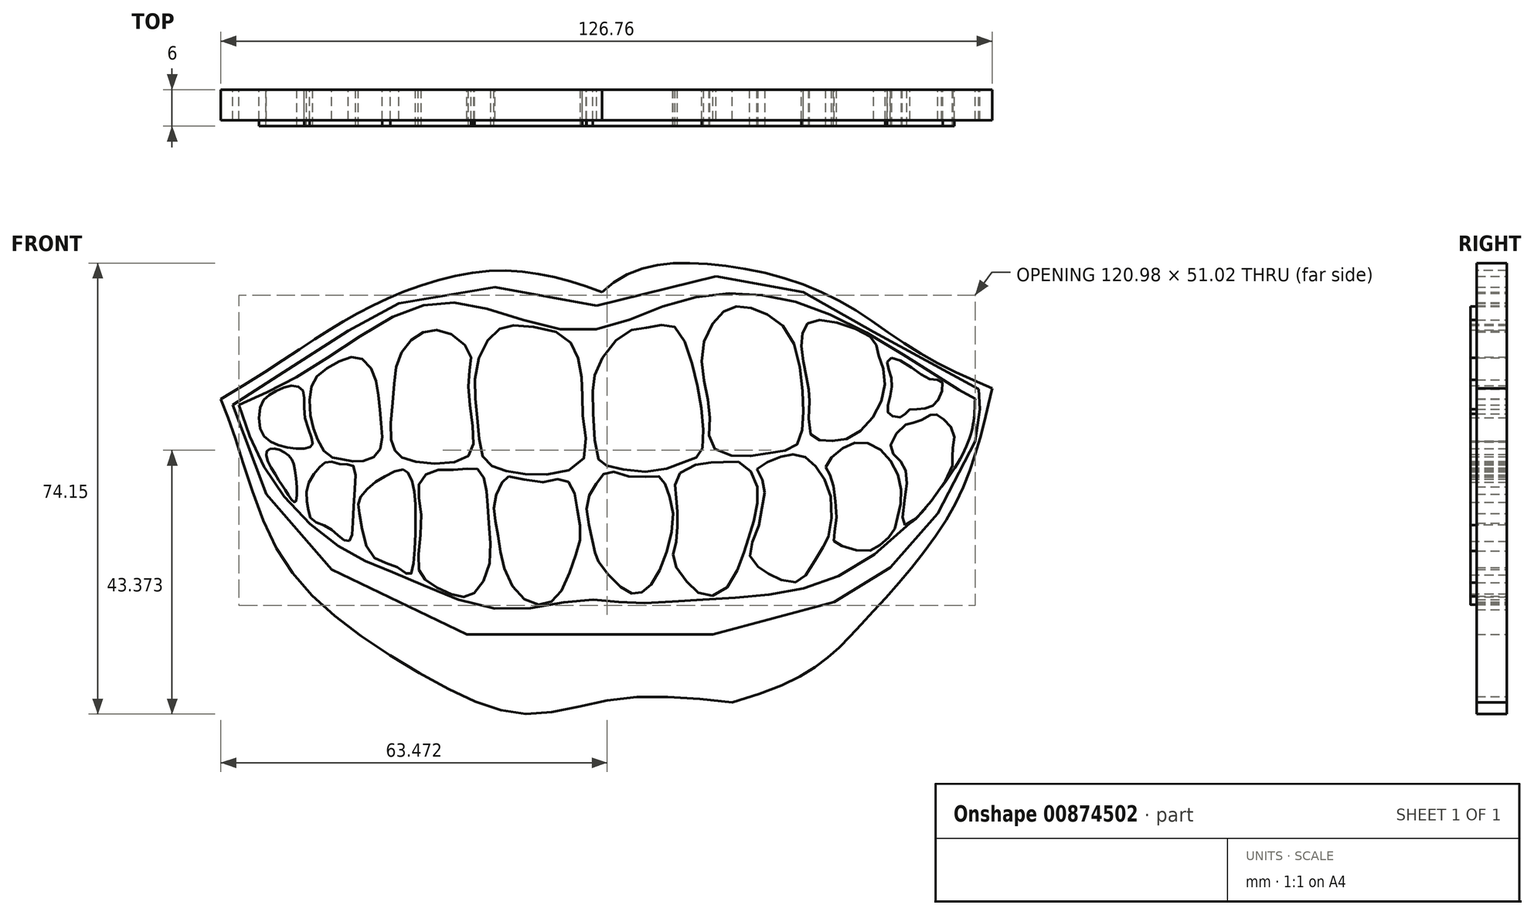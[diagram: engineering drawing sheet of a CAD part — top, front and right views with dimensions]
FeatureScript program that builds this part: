
annotation { "Feature Type Name" : "Feature", "Feature Type Description" : "" }
export const myFeature = defineFeature(function(context is Context, id is Id, definition is map)
    precondition{}
    {
        {
            var Q0;
            Q0=qCreatedBy(makeId("Front.planeOp"),FACE);
            var sketch = newSketch(context, id + "F0", { "sketchPlane" : qUnion([Q0])});
            skFitSpline(sketch, "E0", {"points": [v(0, 53.18) * mm, v(23.75, 67.94) * mm, v(44.07, 74.21) * mm, v(62.66, 70.72) * mm], "startDerivative": vector(93.7, 55.72) * mm, "endDerivative": vector(60.4, -23.03) * mm});
            skFitSpline(sketch, "E1", {"points": [v(126.76, 54.96) * mm, v(114.63, 60.86) * mm, v(103.77, 68.1) * mm, v(91.61, 73.34) * mm, v(78.85, 75.44) * mm, v(69.82, 74.76) * mm, v(62.66, 70.72) * mm], "startDerivative": vector(-69.64, 30.18) * mm, "endDerivative": vector(-38.87, -41.98) * mm});
            skFitSpline(sketch, "E2", {"points": [v(0, 53.18) * mm, v(2.98, 44.84) * mm, v(8.86, 29.1) * mm, v(20.03, 16.48) * mm, v(38.15, 5.15) * mm, v(51.1, 1.38) * mm, v(65.34, 3.9) * mm, v(84.07, 3.33) * mm], "startDerivative": vector(26.52, -69.74) * mm, "endDerivative": vector(123.22, -12.78) * mm});
            skFitSpline(sketch, "E3", {"points": [v(126.76, 54.96) * mm, v(120.46, 35.47) * mm, v(105, 15.84) * mm, v(84.07, 3.33) * mm], "startDerivative": vector(-14.9, -62.4) * mm, "endDerivative": vector(-111.82, -31.62) * mm});
            skFitSpline(sketch, "E4", {"points": [v(2.98, 52.18) * mm, v(14.75, 58.17) * mm, v(30, 67.51) * mm, v(42.1, 68.47) * mm, v(59.06, 64.37) * mm, v(73.77, 68.8) * mm, v(87.62, 70.4) * mm, v(102.75, 65.85) * mm, v(119.4, 55.87) * mm, v(123.96, 53.22) * mm], "startDerivative": vector(105.78, 47.4) * mm, "endDerivative": vector(55.85, -30.6) * mm});
            skFitSpline(sketch, "E5", {"points": [v(2.98, 52.18) * mm, v(8.53, 39.61) * mm, v(20.03, 28.54) * mm, v(30.2, 23.87) * mm, v(45.83, 18.63) * mm, v(59.41, 20.13) * mm, v(67.57, 19.64) * mm, v(77.35, 20.11) * mm, v(90.4, 21.05) * mm, v(106.3, 26.86) * mm, v(122.29, 44.84) * mm, v(123.96, 53.22) * mm], "startDerivative": vector(45.77, -138.86) * mm, "endDerivative": vector(2.36, 104.45) * mm});
            skSolve(sketch);
        }
        {
            var Q0;
            Q0=qSketchRegion(id+"F0",true);
            extrude(context, id + "F1", {"entities" : qUnion([Q0]), "depth" : 5 * mm, "offsetDistance" : 25 * mm});
        }
        {
            var Q0;
            Q0=qCreatedBy(makeId("Front.planeOp"),FACE);
            var sketch = newSketch(context, id + "F2", { "sketchPlane" : qUnion([Q0])});
            skFitSpline(sketch, "E6", {"points": [v(13.53, 54.53) * mm, v(13.72, 50.73) * mm, v(15.07, 46.21) * mm, v(14.78, 45.4) * mm, v(12.9, 45.02) * mm, v(9.13, 45.7) * mm, v(6.62, 47.84) * mm, v(6.75, 52.55) * mm, v(8.76, 54.31) * mm, v(11.77, 55.38) * mm, v(13.53, 54.53) * mm]});
            skFitSpline(sketch, "E7", {"points": [v(15.91, 46.46) * mm, v(17.67, 43.89) * mm, v(20.06, 43.26) * mm, v(22.32, 42.88) * mm, v(24.83, 43.48) * mm, v(26.34, 45.36) * mm, v(26.34, 49.16) * mm, v(25.91, 53.4) * mm, v(24.95, 57.73) * mm, v(22.6, 60.01) * mm, v(19.54, 59.41) * mm, v(16.05, 57.19) * mm, v(14.73, 54.54) * mm, v(14.85, 49.67) * mm, v(15.91, 46.46) * mm]});
            skFitSpline(sketch, "E8", {"points": [v(28.62, 44.69) * mm, v(29.89, 43.48) * mm, v(34.59, 42.6) * mm, v(40.26, 43.48) * mm, v(41.53, 46.18) * mm, v(40.86, 52.9) * mm, v(40.86, 57.98) * mm, v(40.94, 60.82) * mm, v(37.58, 63.95) * mm, v(34, 64.4) * mm, v(31, 62.61) * mm, v(28.91, 58.88) * mm, v(28.32, 53.8) * mm, v(27.87, 47.23) * mm, v(28.62, 44.69) * mm]});
            skFitSpline(sketch, "E9", {"points": [v(44.52, 42.15) * mm, v(48.03, 41.1) * mm, v(54.6, 40.88) * mm, v(59.68, 43.48) * mm, v(59.53, 50.07) * mm, v(59.38, 55.52) * mm, v(58.48, 60.67) * mm, v(55.8, 63.88) * mm, v(48.94, 65.26) * mm, v(45.8, 64.69) * mm, v(42.94, 61.26) * mm, v(41.71, 55.2) * mm, v(42.18, 49.9) * mm, v(42.88, 44.16) * mm, v(44.52, 42.15) * mm]});
            skFitSpline(sketch, "E10", {"points": [v(62.1, 43.24) * mm, v(63.7, 42.16) * mm, v(70.98, 41.29) * mm, v(76.92, 43.14) * mm, v(78.87, 44.25) * mm, v(79.15, 50) * mm, v(77.48, 58.9) * mm, v(74.32, 65.2) * mm, v(70.8, 65.02) * mm, v(66.53, 64.1) * mm, v(61.8, 58.16) * mm, v(61.16, 52.97) * mm, v(62.1, 43.24) * mm]});
            skFitSpline(sketch, "E11", {"points": [v(84.75, 68.4) * mm, v(81.88, 66.9) * mm, v(79.19, 61.72) * mm, v(79.56, 55.52) * mm, v(80.4, 49.9) * mm, v(80.67, 45.49) * mm, v(85.3, 43.73) * mm, v(90.69, 44.38) * mm, v(94.4, 45.4) * mm, v(95.6, 48.73) * mm, v(95.51, 55.52) * mm, v(93.28, 64.1) * mm, v(88.46, 67.65) * mm, v(84.75, 68.4) * mm]});
            skFitSpline(sketch, "E12", {"points": [v(96.73, 52.86) * mm, v(97, 47.25) * mm, v(99.29, 46.31) * mm, v(103.34, 46.8) * mm, v(107.76, 51.18) * mm, v(109.12, 56.92) * mm, v(107.97, 60.88) * mm, v(107.42, 62.7) * mm, v(102.85, 65.25) * mm, v(97.09, 66) * mm, v(95.6, 64.1) * mm, v(95.6, 60.25) * mm, v(96.52, 55.52) * mm, v(96.73, 52.86) * mm]});
            skFitSpline(sketch, "E13", {"points": [v(110.18, 59.97) * mm, v(114.14, 57.92) * mm, v(117.02, 56.33) * mm, v(118.46, 56.1) * mm, v(118.25, 53.68) * mm, v(116.74, 51.94) * mm, v(114.5, 51.53) * mm, v(112.9, 51.3) * mm, v(112, 50.26) * mm, v(110.2, 50.45) * mm, v(109.56, 51.32) * mm, v(110.06, 53.92) * mm, v(110.15, 56.8) * mm, v(109.52, 59.03) * mm, v(110.18, 59.97) * mm]});
            skFitSpline(sketch, "E14", {"points": [v(11.17, 43.89) * mm, v(12.2, 41.1) * mm, v(12.24, 36.22) * mm, v(11.06, 37.44) * mm, v(9.13, 40.43) * mm, v(7.44, 44.3) * mm, v(8.64, 45.02) * mm, v(11.17, 43.89) * mm]});
            skFitSpline(sketch, "E15", {"points": [v(21.14, 29.83) * mm, v(21.72, 34.48) * mm, v(21.79, 42.16) * mm, v(20.1, 42.4) * mm, v(17.67, 42.88) * mm, v(16.05, 41.78) * mm, v(14.24, 38.78) * mm, v(14.3, 35.25) * mm, v(15.07, 33.28) * mm, v(17.67, 32.08) * mm, v(19.72, 30.35) * mm, v(21.14, 29.83) * mm]});
            skFitSpline(sketch, "E16", {"points": [v(30.73, 41.1) * mm, v(31.74, 38.4) * mm, v(31.98, 33.3) * mm, v(31.73, 26.51) * mm, v(31, 24.29) * mm, v(28.91, 25.6) * mm, v(24.83, 27.42) * mm, v(22.77, 34.48) * mm, v(22.7, 36.6) * mm, v(24.54, 38.83) * mm, v(27.44, 40.73) * mm, v(29.89, 41.6) * mm, v(30.73, 41.1) * mm]});
            skFitSpline(sketch, "E17", {"points": [v(42.2, 41.68) * mm, v(43.53, 39.08) * mm, v(43.93, 34.2) * mm, v(44.07, 25.72) * mm, v(41.16, 20.94) * mm, v(38.36, 20.92) * mm, v(33.92, 23.23) * mm, v(32.45, 25.84) * mm, v(32.94, 33.79) * mm, v(32.49, 38.99) * mm, v(34.7, 41.3) * mm, v(39.33, 41.6) * mm, v(42.2, 41.68) * mm]});
            skFitSpline(sketch, "E18", {"points": [v(47.25, 40.47) * mm, v(52.4, 39.48) * mm, v(55.99, 40.03) * mm, v(57.7, 38.78) * mm, v(58.62, 34.68) * mm, v(59.1, 30.71) * mm, v(58.05, 26.74) * mm, v(55.52, 21) * mm, v(52.99, 19.42) * mm, v(49.52, 20.54) * mm, v(46.48, 25.63) * mm, v(45.68, 30.17) * mm, v(44.97, 33.94) * mm, v(45.02, 36.7) * mm, v(46.29, 39.65) * mm, v(47.25, 40.47) * mm]});
            skFitSpline(sketch, "E19", {"points": [v(62.1, 26.4) * mm, v(65.59, 22.35) * mm, v(68.22, 21.16) * mm, v(70.18, 22.1) * mm, v(72.87, 26.9) * mm, v(74.31, 34.2) * mm, v(73.13, 38.88) * mm, v(72.04, 40.46) * mm, v(67.8, 40.35) * mm, v(63.63, 41.25) * mm, v(62, 39.64) * mm, v(60.28, 36.67) * mm, v(60.56, 32.18) * mm, v(61.47, 28.08) * mm, v(62.1, 26.4) * mm]});
            skFitSpline(sketch, "E20", {"points": [v(75.5, 41.02) * mm, v(74.65, 38.62) * mm, v(74.97, 35.94) * mm, v(75.02, 32.76) * mm, v(74.73, 29.26) * mm, v(74.31, 26.9) * mm, v(76.28, 23.51) * mm, v(79.22, 20.96) * mm, v(82.79, 21.8) * mm, v(85.58, 26.9) * mm, v(86.81, 30.54) * mm, v(88.12, 35.59) * mm, v(87.94, 39.62) * mm, v(85.4, 42.75) * mm, v(82.06, 42.72) * mm, v(79.69, 42.72) * mm, v(75.5, 41.02) * mm]});
            skFitSpline(sketch, "E21", {"points": [v(88.12, 41.63) * mm, v(89.22, 39.45) * mm, v(89.15, 36.51) * mm, v(88.12, 31.49) * mm, v(86.94, 27.61) * mm, v(88.64, 25.34) * mm, v(90.8, 24.02) * mm, v(94.25, 23.02) * mm, v(96.37, 24.55) * mm, v(98.81, 28.54) * mm, v(99.9, 30.62) * mm, v(100.18, 37.32) * mm, v(98.19, 41.57) * mm, v(95.75, 43.77) * mm, v(93.22, 44.03) * mm, v(90.69, 43.13) * mm, v(88.12, 41.63) * mm]});
            skFitSpline(sketch, "E22", {"points": [v(99.44, 41.98) * mm, v(101.2, 44.38) * mm, v(104.48, 46.05) * mm, v(107.95, 45.2) * mm, v(110.88, 41.6) * mm, v(111.85, 37.32) * mm, v(111.18, 33.59) * mm, v(110.42, 31.17) * mm, v(108.52, 29.32) * mm, v(106.28, 28.2) * mm, v(102.13, 29.03) * mm, v(100.73, 29.97) * mm, v(101.09, 32.23) * mm, v(100.9, 37.32) * mm, v(100.18, 40.58) * mm, v(99.44, 41.98) * mm]});
            skFitSpline(sketch, "E23", {"points": [v(112.46, 32.44) * mm, v(120.07, 41.6) * mm, v(120.21, 44.38) * mm, v(120.43, 47.74) * mm, v(118.2, 50.28) * mm, v(117.02, 50.71) * mm, v(114.5, 49.43) * mm, v(112.66, 49) * mm, v(110.06, 45.2) * mm, v(111.85, 42.83) * mm, v(112.64, 38.24) * mm, v(112.46, 32.44) * mm]});
            skSolve(sketch);
        }
        {
            var Q0;
            Q0=qSketchRegion(id+"F2",true);
            extrude(context, id + "F3", {"entities" : qUnion([Q0]), "operationType" : NewBodyOperationType.ADD, "depth" : 6 * mm, "offsetDistance" : 25 * mm});
        }
        {
            var Q0;
            Q0=makeQuery(id+"F3.boolean.opBoolean","MERGE",FACE,{"derivedFrom":[makeQuery(id+"F1.opExtrude","CAP_FACE",FACE,{"disambiguationData":[OSD([sQuery(id+"F0.wireOp",EDGE,"E0"),sQuery(id+"F0.wireOp",EDGE,"E1"),sQuery(id+"F0.wireOp",EDGE,"E2"),sQuery(id+"F0.wireOp",EDGE,"E3"),sQuery(id+"F0.wireOp",EDGE,"E4"),sQuery(id+"F0.wireOp",EDGE,"E5")])],"isStart":true}),makeQuery(id+"F3.opExtrude","CAP_FACE",FACE,{"disambiguationData":[OSD([sQuery(id+"F2.wireOp",EDGE,"E23")])],"isStart":true})]});
            var sketch = newSketch(context, id + "F4", { "sketchPlane" : qUnion([Q0])});
            skLineSegment(sketch, "E24", {"start": v(-124.58, 54.81) * mm, "end": v(-107.3, 64.23) * mm});
            skLineSegment(sketch, "E25", {"start": v(-107.3, 64.23) * mm, "end": v(-95.76, 70.72) * mm});
            skLineSegment(sketch, "E26", {"start": v(-95.76, 70.72) * mm, "end": v(-81.4, 73.33) * mm});
            skLineSegment(sketch, "E27", {"start": v(-81.4, 73.33) * mm, "end": v(-61.73, 68.5) * mm});
            skLineSegment(sketch, "E28", {"start": v(-61.73, 68.5) * mm, "end": v(-45.06, 71.56) * mm});
            skLineSegment(sketch, "E29", {"start": v(-45.06, 71.56) * mm, "end": v(-29.22, 68.92) * mm});
            skLineSegment(sketch, "E30", {"start": v(-29.22, 68.92) * mm, "end": v(-20.94, 64.43) * mm});
            skLineSegment(sketch, "E31", {"start": v(-20.94, 64.43) * mm, "end": v(-9.45, 57.03) * mm});
            skLineSegment(sketch, "E32", {"start": v(-9.45, 57.03) * mm, "end": v(-1.92, 52.18) * mm});
            skLineSegment(sketch, "E33", {"start": v(-1.92, 52.18) * mm, "end": v(-7.44, 37.53) * mm});
            skLineSegment(sketch, "E34", {"start": v(-7.44, 37.53) * mm, "end": v(-18.2, 25.13) * mm});
            skLineSegment(sketch, "E35", {"start": v(-18.2, 25.13) * mm, "end": v(-40.4, 14.47) * mm});
            skLineSegment(sketch, "E36", {"start": v(-40.4, 14.47) * mm, "end": v(-80.9, 14.47) * mm});
            skLineSegment(sketch, "E37", {"start": v(-80.9, 14.47) * mm, "end": v(-100.79, 19.8) * mm});
            skLineSegment(sketch, "E38", {"start": v(-100.79, 19.8) * mm, "end": v(-110.02, 25.48) * mm});
            skLineSegment(sketch, "E39", {"start": v(-110.02, 25.48) * mm, "end": v(-117.84, 34.36) * mm});
            skLineSegment(sketch, "E40", {"start": v(-117.84, 34.36) * mm, "end": v(-123.96, 46.26) * mm});
            skLineSegment(sketch, "E41", {"start": v(-123.96, 46.26) * mm, "end": v(-124.76, 51.49) * mm});
            skLineSegment(sketch, "E42", {"start": v(-124.76, 51.49) * mm, "end": v(-124.58, 54.81) * mm});
            skSolve(sketch);
        }
        {
            var Q0;
            Q0=qSketchRegion(id+"F4",true);
            extrude(context, id + "F5", {"entities" : qUnion([Q0]), "oppositeDirection" : true, "depth" : 5 * mm, "offsetDistance" : 25 * mm});
        }
    });
